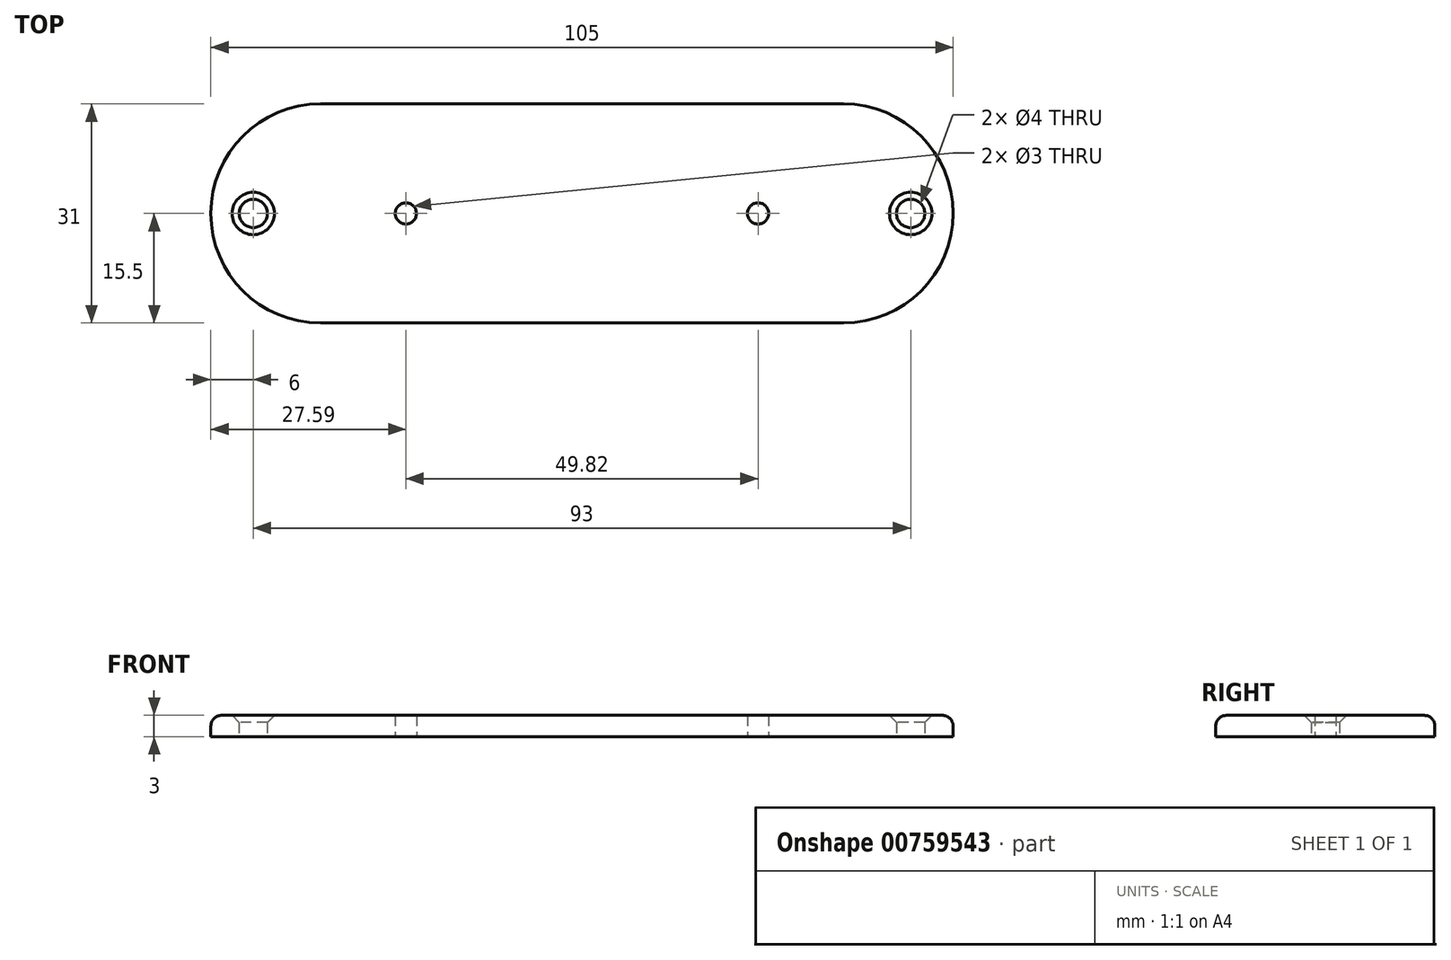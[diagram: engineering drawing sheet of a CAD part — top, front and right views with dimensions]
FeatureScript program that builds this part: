
annotation { "Feature Type Name" : "Feature", "Feature Type Description" : "" }
export const myFeature = defineFeature(function(context is Context, id is Id, definition is map)
    precondition{}
    {
        {
            var Q0;
            Q0=qCreatedBy(makeId("Top.planeOp"),FACE);
            var sketch = newSketch(context, id + "F0", { "sketchPlane" : qUnion([Q0])});
            skLineSegment(sketch, "E0.bottom", {"start": v(-37, 15.5) * mm, "end": v(37, 15.5) * mm});
            skLineSegment(sketch, "E0.top", {"start": v(-37, -15.5) * mm, "end": v(37, -15.5) * mm});
            skPoint(sketch, "E0.middle", {"position": v(0, 0) * mm});
            skArc(sketch, "E1", {"start": v(-37, 15.5) * mm, "mid": v(-52.5, 0) * mm, "end": v(-37, -15.5) * mm});
            skPoint(sketch, "E2.orphan", {"position": v(-52.5, 15.5) * mm});
            skPoint(sketch, "E3.orphan", {"position": v(-52.5, -15.5) * mm});
            skArc(sketch, "E4.MirrorCS", {"start": v(37, 15.5) * mm, "mid": v(52.5, 0) * mm, "end": v(37, -15.5) * mm});
            skPoint(sketch, "E5.orphan", {"position": v(52.5, 15.5) * mm});
            skPoint(sketch, "E0.right.end.orphan", {"position": v(52.5, -15.5) * mm});
            skCircle(sketch, "E6", {"center": v(-46.5, 0) * mm, "radius": 2 * mm});
            skCircle(sketch, "E7", {"center": v(-24.9, 0) * mm, "radius": 1.5 * mm});
            skCircle(sketch, "E8.MirrorC", {"center": v(24.9, 0) * mm, "radius": 1.5 * mm});
            skCircle(sketch, "E9.MirrorC", {"center": v(46.5, 0) * mm, "radius": 2 * mm});
            skSolve(sketch);
        }
        {
            var Q0;
            Q0 = qSketchRegion(id + "F0", true);
            extrude(context, id + "F1", {"entities" : qUnion([Q0]), "depth" : 3 * mm, "offsetDistance" : 25 * mm});
        }
        {
            var Q0;
            Q0=makeQuery(id+"F1.opExtrude","CAP_EDGE",EDGE,{"disambiguationData":[OSD([sQuery(id+"F0.wireOp",EDGE,"E0.bottom")])],"isStart":false});
            fillet(context, id + "F2", {"entities" : qUnion([Q0]), "radius" : 1.5 * mm, "tangentPropagation" : true, "allowEdgeOverflow" : false});
        }
        {
            var Q0;
            Q0=makeQuery(id+"F1.opExtrude","CAP_EDGE",EDGE,{"disambiguationData":[OSD([sQuery(id+"F0.wireOp",EDGE,"E6")])],"isStart":false});
            var Q1;
            Q1=makeQuery(id+"F1.opExtrude","CAP_EDGE",EDGE,{"disambiguationData":[OSD([sQuery(id+"F0.wireOp",EDGE,"E9.MirrorC")])],"isStart":false});
            chamfer(context, id + "F3", {"entities" : qUnion([Q0, Q1]), "width" : 1 * mm, "tangentPropagation" : true});
        }
    });
